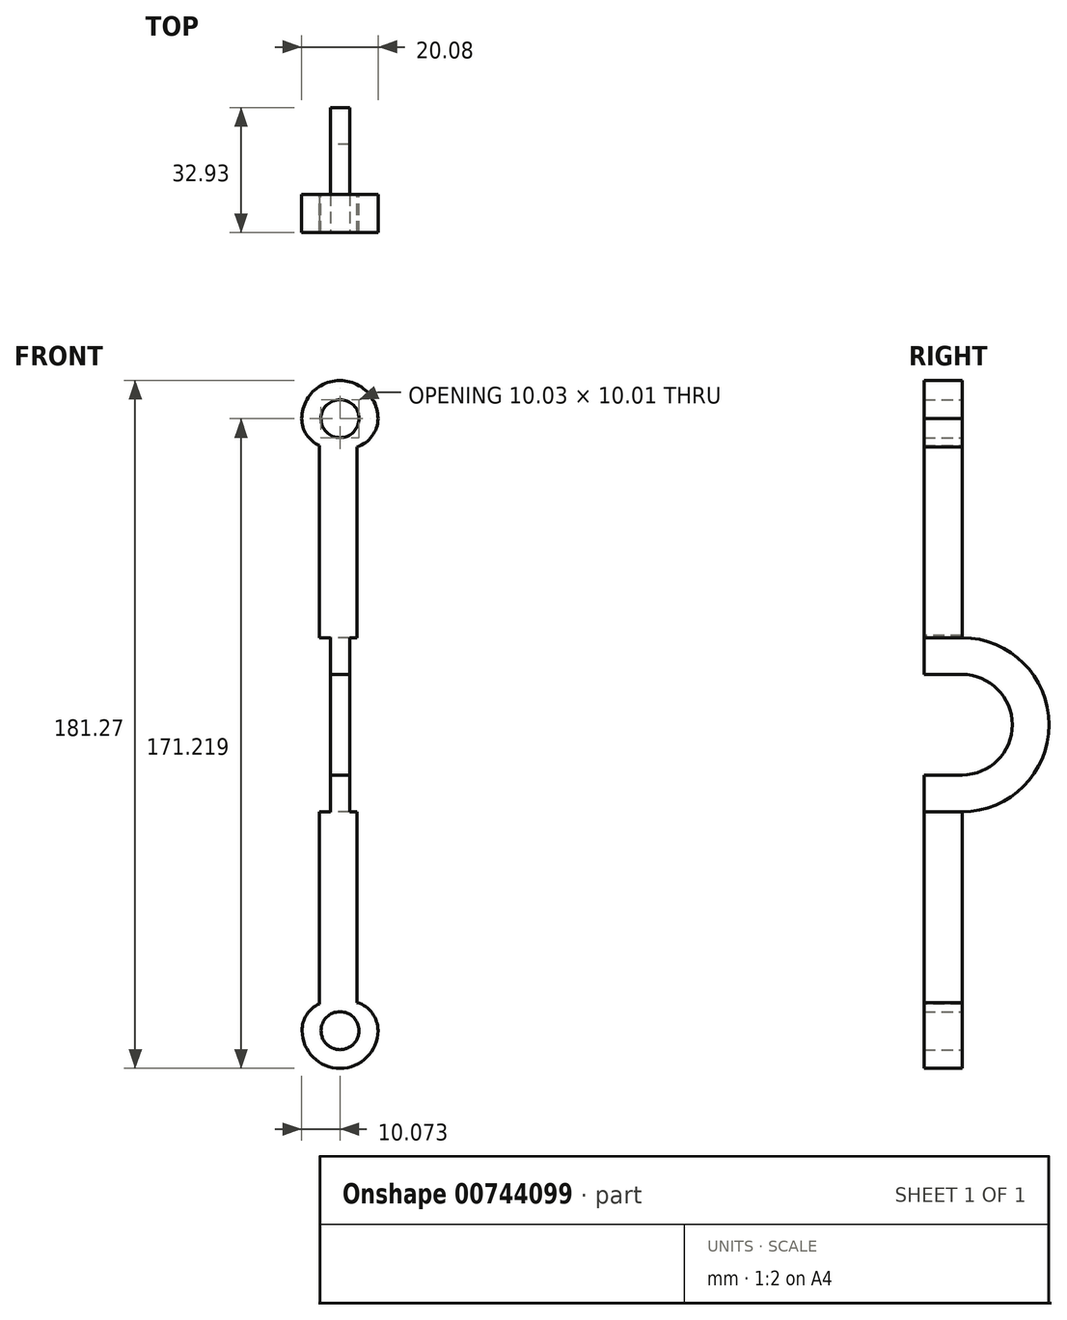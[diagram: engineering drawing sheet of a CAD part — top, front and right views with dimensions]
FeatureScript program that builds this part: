
annotation { "Feature Type Name" : "Feature", "Feature Type Description" : "" }
export const myFeature = defineFeature(function(context is Context, id is Id, definition is map)
    precondition{}
    {
        {
            var Q0;
            Q0=qCreatedBy(makeId("Right.planeOp"),FACE);
            var sketch = newSketch(context, id + "F0", { "sketchPlane" : qUnion([Q0])});
            skLineSegment(sketch, "E0", {"start": v(0, 45.86) * mm, "end": v(0, 36.18) * mm});
            skLineSegment(sketch, "E1", {"start": v(0, 0) * mm, "end": v(0, 9.68) * mm});
            skArc(sketch, "E2", {"start": v(0, 9.68) * mm, "mid": v(13.25, 22.93) * mm, "end": v(0, 36.18) * mm});
            skArc(sketch, "E3", {"start": v(0, 0) * mm, "mid": v(22.93, 22.93) * mm, "end": v(0, 45.86) * mm});
            skLineSegment(sketch, "E4", {"start": v(0, 45.86) * mm, "end": v(0, 95.86) * mm});
            skLineSegment(sketch, "E5", {"start": v(0, 0) * mm, "end": v(0, -50) * mm});
            skLineSegment(sketch, "E6", {"start": v(0, 36.18) * mm, "end": v(0, 9.68) * mm});
            skPoint(sketch, "E7.endSnap0", {"position": v(0, 41.02) * mm});
            skLineSegment(sketch, "E8", {"start": v(0, 9.68) * mm, "end": v(-10, 9.68) * mm});
            skLineSegment(sketch, "E9", {"start": v(0, 0) * mm, "end": v(-10, 0) * mm});
            skLineSegment(sketch, "E10", {"start": v(0, 36.18) * mm, "end": v(-10, 36.18) * mm});
            skLineSegment(sketch, "E11", {"start": v(0, 45.86) * mm, "end": v(-10, 45.86) * mm});
            skLineSegment(sketch, "E12", {"start": v(-10, 45.86) * mm, "end": v(-10, 36.18) * mm});
            skLineSegment(sketch, "E13", {"start": v(-10, 9.68) * mm, "end": v(-10, 0) * mm});
            skLineSegment(sketch, "E14", {"start": v(-10, 0) * mm, "end": v(-10, -50) * mm});
            skLineSegment(sketch, "E15", {"start": v(0, -50) * mm, "end": v(-10, -50) * mm});
            skPoint(sketch, "E16.start.orphan", {"position": v(3.95, 0.34) * mm});
            skPoint(sketch, "E17.end.orphan", {"position": v(3.95, -50) * mm});
            skLineSegment(sketch, "E18", {"start": v(-10, 45.86) * mm, "end": v(-10, 95.86) * mm});
            skLineSegment(sketch, "E19", {"start": v(-10, 95.86) * mm, "end": v(0, 95.86) * mm});
            skPoint(sketch, "E20.end.orphan", {"position": v(3.95, 95.86) * mm});
            skSolve(sketch);
        }
        {
            var Q0;
            Q0=makeQuery(id+"F0.imprint","IMPRINT",FACE,{"disambiguationData":[TD([[makeQuery(id+"F0.imprint","IMPRINT",EDGE,{"derivedFrom":sQuery(id+"F0.wireOp",EDGE,"E0")}),1.0]])]});
            var Q1;
            Q1=makeQuery(id+"F0.imprint","IMPRINT",FACE,{"disambiguationData":[TD([[makeQuery(id+"F0.imprint","IMPRINT",EDGE,{"derivedFrom":sQuery(id+"F0.wireOp",EDGE,"E5")}),-1.0]])]});
            var Q2;
            Q2=makeQuery(id+"F0.imprint","IMPRINT",FACE,{"disambiguationData":[TD([[makeQuery(id+"F0.imprint","IMPRINT",EDGE,{"derivedFrom":sQuery(id+"F0.wireOp",EDGE,"E1")}),1.0]])]});
            var Q3;
            Q3=makeQuery(id+"F0.imprint","IMPRINT",FACE,{"disambiguationData":[TD([[makeQuery(id+"F0.imprint","IMPRINT",EDGE,{"derivedFrom":sQuery(id+"F0.wireOp",EDGE,"E0")}),-1.0]])]});
            var Q4;
            Q4=makeQuery(id+"F0.imprint","IMPRINT",FACE,{"disambiguationData":[TD([[makeQuery(id+"F0.imprint","IMPRINT",EDGE,{"derivedFrom":sQuery(id+"F0.wireOp",EDGE,"E4")}),1.0]])]});
            extrude(context, id + "F1", {"entities" : qUnion([Q0, Q1, Q2, Q3, Q4]), "depth" : 4 * mm, "offsetDistance" : 25 * mm});
        }
        {
            var Q0;
            {var subQ0=sQuery(id+"F0.wireOp",EDGE,"E4");Q0=makeQuery(id+"F0.imprint","IMPRINT",FACE,{"disambiguationData":[TD([[makeQuery(id+"F0.imprint","IMPRINT",EDGE,{"derivedFrom":subQ0}),-1.0]])]});}
            var Q1;
            {var subQ0=sQuery(id+"F0.wireOp",EDGE,"E5");Q1=makeQuery(id+"F0.imprint","IMPRINT",FACE,{"disambiguationData":[TD([[makeQuery(id+"F0.imprint","IMPRINT",EDGE,{"derivedFrom":subQ0}),1.0]])]});}
            var Q2;
            {var subQ3=sQuery(id+"F0.wireOp",EDGE,"E0");Q2=makeQuery(id+"F0.imprint","IMPRINT",FACE,{"disambiguationData":[TD([[makeQuery(id+"F0.imprint","IMPRINT",EDGE,{"derivedFrom":subQ3}),1.0]])]});}
            extrude(context, id + "F2", {"entities" : qUnion([Q0, Q1, Q2]), "operationType" : NewBodyOperationType.ADD, "depth" : 5 * mm, "offsetDistance" : 25 * mm});
        }
        {
            var Q0;
            Q0=qCreatedBy(makeId("Front.planeOp"),FACE);
            var sketch = newSketch(context, id + "F3", { "sketchPlane" : qUnion([Q0])});
            skLineSegment(sketch, "E21", {"start": v(7.5, 103.58) * mm, "end": v(12.5, 103.58) * mm});
            skLineSegment(sketch, "E22", {"start": v(-2.52, 103.58) * mm, "end": v(-7.58, 103.58) * mm});
            skArc(sketch, "E23", {"start": v(-7.58, 103.58) * mm, "mid": v(-5.36, 98.18) * mm, "end": v(0, 95.86) * mm});
            skArc(sketch, "E24", {"start": v(5.02, 95.83) * mm, "mid": v(10.3, 98.22) * mm, "end": v(12.5, 103.58) * mm});
            skArc(sketch, "E25", {"start": v(-2.52, 103.58) * mm, "mid": v(2.5, 98.58) * mm, "end": v(7.5, 103.58) * mm});
            skLineSegment(sketch, "E26", {"start": v(0, 95.86) * mm, "end": v(5.02, 95.83) * mm});
            skLineSegment(sketch, "E27", {"start": v(-2.5, -57.69) * mm, "end": v(-7.5, -57.69) * mm});
            skLineSegment(sketch, "E28", {"start": v(7.48, -57.69) * mm, "end": v(12.5, -57.69) * mm});
            skArc(sketch, "E29", {"start": v(0, -49.95) * mm, "mid": v(-5.34, -52.28) * mm, "end": v(-7.5, -57.69) * mm});
            skArc(sketch, "E30", {"start": v(12.5, -57.69) * mm, "mid": v(10.28, -52.25) * mm, "end": v(4.88, -49.95) * mm});
            skArc(sketch, "E31", {"start": v(7.48, -57.69) * mm, "mid": v(2.49, -52.7) * mm, "end": v(-2.5, -57.69) * mm});
            skLineSegment(sketch, "E32", {"start": v(0, -49.95) * mm, "end": v(4.88, -49.95) * mm});
            skArc(sketch, "E33", {"start": v(-2.5, -57.69) * mm, "mid": v(2.49, -62.7) * mm, "end": v(7.48, -57.69) * mm});
            skArc(sketch, "E34", {"start": v(-7.5, -57.69) * mm, "mid": v(2.5, -67.63) * mm, "end": v(12.5, -57.69) * mm});
            skArc(sketch, "E35", {"start": v(7.5, 103.58) * mm, "mid": v(2.5, 108.6) * mm, "end": v(-2.52, 103.58) * mm});
            skArc(sketch, "E36", {"start": v(12.5, 103.58) * mm, "mid": v(2.46, 113.64) * mm, "end": v(-7.58, 103.58) * mm});
            skSolve(sketch);
        }
        {
            var Q0;
            Q0=makeQuery(id+"F3.imprint","IMPRINT",FACE,{"disambiguationData":[TD([[makeQuery(id+"F3.imprint","IMPRINT",EDGE,{"derivedFrom":sQuery(id+"F3.wireOp",EDGE,"E27")}),-1.0]])]});
            var Q1;
            Q1=makeQuery(id+"F3.imprint","IMPRINT",FACE,{"disambiguationData":[TD([[makeQuery(id+"F3.imprint","IMPRINT",EDGE,{"derivedFrom":sQuery(id+"F3.wireOp",EDGE,"E21")}),-1.0]])]});
            var Q2;
            Q2=makeQuery(id+"F3.imprint","IMPRINT",FACE,{"disambiguationData":[TD([[makeQuery(id+"F3.imprint","IMPRINT",EDGE,{"derivedFrom":sQuery(id+"F3.wireOp",EDGE,"E21")}),1.0]])]});
            var Q3;
            Q3=makeQuery(id+"F1.opExtrude","SWEPT_FACE",FACE,{"disambiguationData":[OSD([sQuery(id+"F0.wireOp",EDGE,"E13"),sQuery(id+"F0.wireOp",EDGE,"E14")])]});
            var Q4;
            Q4=makeQuery(id+"F1.opExtrude","SWEPT_FACE",FACE,{"disambiguationData":[OSD([sQuery(id+"F0.wireOp",EDGE,"E12"),sQuery(id+"F0.wireOp",EDGE,"E18")])]});
            extrude(context, id + "F4", {"entities" : qUnion([Q0, Q1, Q2]), "operationType" : NewBodyOperationType.ADD, "endBound" : BoundingType.UP_TO_SURFACE, "depth" : 0 * mm, "endBoundEntityFace" : qUnion([Q3]), "offsetDistance" : 25 * mm});
        }
        {
            var Q0;
            Q0=makeQuery(id+"F0.imprint","IMPRINT",FACE,{"disambiguationData":[TD([[makeQuery(id+"F0.imprint","IMPRINT",EDGE,{"derivedFrom":sQuery(id+"F0.wireOp",EDGE,"E1")}),1.0]])]});
            var Q1;
            {var subQ3=sQuery(id+"F0.wireOp",EDGE,"E0");Q1=makeQuery(id+"F0.imprint","IMPRINT",FACE,{"disambiguationData":[TD([[makeQuery(id+"F0.imprint","IMPRINT",EDGE,{"derivedFrom":subQ3}),1.0]])]});}
            var Q2;
            Q2=makeQuery(id+"F0.imprint","IMPRINT",FACE,{"disambiguationData":[TD([[makeQuery(id+"F0.imprint","IMPRINT",EDGE,{"derivedFrom":sQuery(id+"F0.wireOp",EDGE,"E0")}),-1.0]])]});
            var Q3;
            {var subQ0=sQuery(id+"F0.wireOp",EDGE,"E4");Q3=makeQuery(id+"F0.imprint","IMPRINT",FACE,{"disambiguationData":[TD([[makeQuery(id+"F0.imprint","IMPRINT",EDGE,{"derivedFrom":subQ0}),-1.0]])]});}
            var Q4;
            {var subQ0=sQuery(id+"F0.wireOp",EDGE,"E5");Q4=makeQuery(id+"F0.imprint","IMPRINT",FACE,{"disambiguationData":[TD([[makeQuery(id+"F0.imprint","IMPRINT",EDGE,{"derivedFrom":subQ0}),1.0]])]});}
            extrude(context, id + "F5", {"entities" : qUnion([Q0, Q1, Q2, Q3, Q4]), "operationType" : NewBodyOperationType.ADD, "depth" : 5 * mm, "offsetDistance" : 25 * mm});
        }
        {
            var Q0;
            Q0=makeQuery(id+"F3.imprint","IMPRINT",FACE,{"disambiguationData":[TD([[makeQuery(id+"F3.imprint","IMPRINT",EDGE,{"derivedFrom":sQuery(id+"F3.wireOp",EDGE,"E27")}),1.0]])]});
            extrude(context, id + "F6", {"entities" : qUnion([Q0]), "operationType" : NewBodyOperationType.ADD, "depth" : 10 * mm, "offsetDistance" : 25 * mm});
        }
        {
            var Q0;
            Q0=makeQuery(id+"F0.imprint","IMPRINT",FACE,{"disambiguationData":[TD([[makeQuery(id+"F0.imprint","IMPRINT",EDGE,{"derivedFrom":sQuery(id+"F0.wireOp",EDGE,"E0")}),1.0]])]});
            var Q1;
            Q1=makeQuery(id+"F0.imprint","IMPRINT",FACE,{"disambiguationData":[TD([[makeQuery(id+"F0.imprint","IMPRINT",EDGE,{"derivedFrom":sQuery(id+"F0.wireOp",EDGE,"E1")}),1.0]])]});
            var Q2;
            Q2=makeQuery(id+"F0.imprint","IMPRINT",FACE,{"disambiguationData":[TD([[makeQuery(id+"F0.imprint","IMPRINT",EDGE,{"derivedFrom":sQuery(id+"F0.wireOp",EDGE,"E0")}),-1.0]])]});
            extrude(context, id + "F7", {"entities" : qUnion([Q0, Q1, Q2]), "operationType" : NewBodyOperationType.ADD, "depth" : 4 * mm, "offsetDistance" : 25 * mm});
        }
        {
            var Q0;
            {var subQ0=sQuery(id+"F3.wireOp",EDGE,"E28");var subQ1=sQuery(id+"F3.wireOp",EDGE,"E27");var subQ2=sQuery(id+"F0.wireOp",EDGE,"E13");Q0=makeQuery(id+"F6.boolean.opBoolean","MERGE",FACE,{"derivedFrom":[makeQuery(id+"F5.boolean.opBoolean","MERGE",FACE,{"derivedFrom":[makeQuery(id+"F4.boolean.opBoolean","MERGE",FACE,{"derivedFrom":[makeQuery(id+"F1.opExtrude","SWEPT_FACE",FACE,{"disambiguationData":[OSD([subQ2,sQuery(id+"F0.wireOp",EDGE,"E14")])]}),makeQuery(id+"F4.opExtrude","CAP_FACE",FACE,{"disambiguationData":[OSD([subQ1,subQ0,sQuery(id+"F3.wireOp",EDGE,"E29"),sQuery(id+"F3.wireOp",EDGE,"E30"),sQuery(id+"F3.wireOp",EDGE,"E31"),sQuery(id+"F3.wireOp",EDGE,"E32")])],"isStart":false})]}),makeQuery(id+"F5.opExtrude","SWEPT_FACE",FACE,{"disambiguationData":[OSD([subQ2])]})]}),makeQuery(id+"F6.opExtrude","CAP_FACE",FACE,{"disambiguationData":[OSD([subQ1,subQ0,sQuery(id+"F3.wireOp",EDGE,"E33"),sQuery(id+"F3.wireOp",EDGE,"E34")])],"isStart":false})]});}
            var sketch = newSketch(context, id + "F8", { "sketchPlane" : qUnion([Q0])});
            skLineSegment(sketch, "E37", {"start": v(-3, -2.45) * mm, "end": v(-3, -50.63) * mm});
            skLineSegment(sketch, "E38", {"start": v(7, -2.45) * mm, "end": v(7, -49.95) * mm});
            skLineSegment(sketch, "E39", {"start": v(-3, -2.45) * mm, "end": v(7, -2.45) * mm});
            skLineSegment(sketch, "E40", {"start": v(7, 63.85) * mm, "end": v(7, 46.07) * mm});
            skLineSegment(sketch, "E41", {"start": v(-3, 63.85) * mm, "end": v(-3, 46.44) * mm});
            skLineSegment(sketch, "E42", {"start": v(7, -49.95) * mm, "end": v(7, -50.27) * mm});
            skLineSegment(sketch, "E43", {"start": v(-3, 63.85) * mm, "end": v(-3, 95.87) * mm});
            skLineSegment(sketch, "E44", {"start": v(7, 63.85) * mm, "end": v(7, 95.87) * mm});
            skLineSegment(sketch, "E45", {"start": v(-3, 95.87) * mm, "end": v(-3, 96.56) * mm});
            skLineSegment(sketch, "E46", {"start": v(7, 95.87) * mm, "end": v(7, 96.56) * mm});
            skLineSegment(sketch, "E47", {"start": v(7, 96.56) * mm, "end": v(-3, 96.56) * mm});
            skLineSegment(sketch, "E48", {"start": v(7, -2.45) * mm, "end": v(7, 0) * mm});
            skLineSegment(sketch, "E49", {"start": v(-3, -2.45) * mm, "end": v(-3, 0) * mm});
            skLineSegment(sketch, "E50", {"start": v(-3, 0) * mm, "end": v(7, 0) * mm});
            skLineSegment(sketch, "E51", {"start": v(7, 46.07) * mm, "end": v(7, 45.82) * mm});
            skLineSegment(sketch, "E52", {"start": v(7, 45.82) * mm, "end": v(-3, 45.82) * mm});
            skLineSegment(sketch, "E53", {"start": v(-3, 46.44) * mm, "end": v(-3, 45.82) * mm});
            skLineSegment(sketch, "E54", {"start": v(0, 46.44) * mm, "end": v(0, 45.82) * mm});
            skLineSegment(sketch, "E55", {"start": v(3.94, 46.44) * mm, "end": v(3.94, 45.82) * mm});
            skSolve(sketch);
        }
        {
            var Q0;
            {var subQ2=sQuery(id+"F8.wireOp",EDGE,"E38");Q0=makeQuery(id+"F8.imprint","IMPRINT",FACE,{"disambiguationData":[TD([[makeQuery(id+"F8.imprint","IMPRINT",EDGE,{"derivedFrom":subQ2}),-1.0]])]});}
            var Q1;
            {var subQ0=sQuery(id+"F3.wireOp",EDGE,"E28");var subQ1=sQuery(id+"F3.wireOp",EDGE,"E27");Q1=makeQuery(id+"F6.boolean.opBoolean","MERGE",FACE,{"derivedFrom":[makeQuery(id+"F4.boolean.opBoolean","MERGE",FACE,{"derivedFrom":[makeQuery(id+"F1.opExtrude","SWEPT_FACE",FACE,{"disambiguationData":[OSD([sQuery(id+"F0.wireOp",EDGE,"E5")])]}),makeQuery(id+"F4.opExtrude","CAP_FACE",FACE,{"disambiguationData":[OSD([subQ1,subQ0,sQuery(id+"F3.wireOp",EDGE,"E29"),sQuery(id+"F3.wireOp",EDGE,"E30"),sQuery(id+"F3.wireOp",EDGE,"E31"),sQuery(id+"F3.wireOp",EDGE,"E32")])],"isStart":true})]}),makeQuery(id+"F6.opExtrude","CAP_FACE",FACE,{"disambiguationData":[OSD([subQ1,subQ0,sQuery(id+"F3.wireOp",EDGE,"E33"),sQuery(id+"F3.wireOp",EDGE,"E34")])],"isStart":true})]});}
            extrude(context, id + "F9", {"entities" : qUnion([Q0]), "operationType" : NewBodyOperationType.ADD, "endBound" : BoundingType.UP_TO_SURFACE, "oppositeDirection" : true, "depth" : 25 * mm, "endBoundEntityFace" : qUnion([Q1]), "offsetDistance" : 25 * mm});
        }
        {
            var Q0;
            {var subQ0=sQuery(id+"F8.wireOp",EDGE,"E37");Q0=makeQuery(id+"F8.imprint","IMPRINT",FACE,{"disambiguationData":[TD([[makeQuery(id+"F8.imprint","IMPRINT",EDGE,{"derivedFrom":subQ0}),1.0]])]});}
            var Q1;
            {var subQ0=sQuery(id+"F3.wireOp",EDGE,"E32");var subQ1=sQuery(id+"F3.wireOp",EDGE,"E30");var subQ2=sQuery(id+"F3.wireOp",EDGE,"E28");var subQ3=sQuery(id+"F3.wireOp",EDGE,"E27");Q1=makeQuery(id+"F9.boolean.opBoolean","MERGE",FACE,{"derivedFrom":[makeQuery(id+"F6.boolean.opBoolean","MERGE",FACE,{"derivedFrom":[makeQuery(id+"F4.boolean.opBoolean","MERGE",FACE,{"derivedFrom":[makeQuery(id+"F1.opExtrude","SWEPT_FACE",FACE,{"disambiguationData":[OSD([sQuery(id+"F0.wireOp",EDGE,"E5")])]}),makeQuery(id+"F4.opExtrude","CAP_FACE",FACE,{"disambiguationData":[OSD([subQ3,subQ2,sQuery(id+"F3.wireOp",EDGE,"E29"),subQ1,sQuery(id+"F3.wireOp",EDGE,"E31"),subQ0])],"isStart":true})]}),makeQuery(id+"F6.opExtrude","CAP_FACE",FACE,{"disambiguationData":[OSD([subQ3,subQ2,sQuery(id+"F3.wireOp",EDGE,"E33"),sQuery(id+"F3.wireOp",EDGE,"E34")])],"isStart":true})]}),makeQuery(id+"F9.opExtrude","CAP_FACE",FACE,{"disambiguationData":[OSD([sQuery(id+"F0.wireOp",EDGE,"E13"),sQuery(id+"F0.wireOp",EDGE,"E14"),subQ1,subQ0,sQuery(id+"F8.wireOp",EDGE,"E38"),sQuery(id+"F8.wireOp",EDGE,"E39"),sQuery(id+"F8.wireOp",EDGE,"E42")])],"isStart":false})]});}
            extrude(context, id + "F10", {"entities" : qUnion([Q0]), "operationType" : NewBodyOperationType.ADD, "endBound" : BoundingType.UP_TO_SURFACE, "oppositeDirection" : true, "depth" : 25 * mm, "endBoundEntityFace" : qUnion([Q1]), "offsetDistance" : 25 * mm});
        }
        {
            var Q0;
            Q0=makeQuery(id+"F8.imprint","IMPRINT",FACE,{"disambiguationData":[TD([[makeQuery(id+"F8.imprint","IMPRINT",EDGE,{"derivedFrom":sQuery(id+"F8.wireOp",EDGE,"E41")}),1.0]])]});
            var Q1;
            Q1=makeQuery(id+"F4.boolean.opBoolean","MERGE",FACE,{"derivedFrom":[makeQuery(id+"F1.opExtrude","SWEPT_FACE",FACE,{"disambiguationData":[OSD([sQuery(id+"F0.wireOp",EDGE,"E4")])]}),makeQuery(id+"F4.opExtrude","CAP_FACE",FACE,{"disambiguationData":[OSD([sQuery(id+"F3.wireOp",EDGE,"E23"),sQuery(id+"F3.wireOp",EDGE,"E24"),sQuery(id+"F3.wireOp",EDGE,"E25"),sQuery(id+"F3.wireOp",EDGE,"E26"),sQuery(id+"F3.wireOp",EDGE,"E35"),sQuery(id+"F3.wireOp",EDGE,"E36")])],"isStart":true})]});
            extrude(context, id + "F11", {"entities" : qUnion([Q0]), "operationType" : NewBodyOperationType.ADD, "endBound" : BoundingType.UP_TO_SURFACE, "oppositeDirection" : true, "depth" : 25 * mm, "endBoundEntityFace" : qUnion([Q1]), "offsetDistance" : 25 * mm});
        }
        {
            var Q0;
            {var subQ3=sQuery(id+"F8.wireOp",EDGE,"E48");Q0=makeQuery(id+"F8.imprint","IMPRINT",FACE,{"disambiguationData":[TD([[makeQuery(id+"F8.imprint","IMPRINT",EDGE,{"derivedFrom":subQ3}),1.0]])]});}
            var Q1;
            {var subQ0=sQuery(id+"F8.wireOp",EDGE,"E49");Q1=makeQuery(id+"F8.imprint","IMPRINT",FACE,{"disambiguationData":[TD([[makeQuery(id+"F8.imprint","IMPRINT",EDGE,{"derivedFrom":subQ0}),-1.0]])]});}
            var Q2;
            {var subQ0=sQuery(id+"F8.wireOp",EDGE,"E39");var subQ1=sQuery(id+"F3.wireOp",EDGE,"E29");var subQ2=sQuery(id+"F0.wireOp",EDGE,"E14");var subQ3=sQuery(id+"F0.wireOp",EDGE,"E13");var subQ4=sQuery(id+"F3.wireOp",EDGE,"E32");var subQ5=sQuery(id+"F3.wireOp",EDGE,"E30");var subQ6=sQuery(id+"F3.wireOp",EDGE,"E28");var subQ7=sQuery(id+"F3.wireOp",EDGE,"E27");Q2=makeQuery(id+"F10.boolean.opBoolean","MERGE",FACE,{"derivedFrom":[makeQuery(id+"F9.boolean.opBoolean","MERGE",FACE,{"derivedFrom":[makeQuery(id+"F6.boolean.opBoolean","MERGE",FACE,{"derivedFrom":[makeQuery(id+"F4.boolean.opBoolean","MERGE",FACE,{"derivedFrom":[makeQuery(id+"F1.opExtrude","SWEPT_FACE",FACE,{"disambiguationData":[OSD([sQuery(id+"F0.wireOp",EDGE,"E5")])]}),makeQuery(id+"F4.opExtrude","CAP_FACE",FACE,{"disambiguationData":[OSD([subQ7,subQ6,subQ1,subQ5,sQuery(id+"F3.wireOp",EDGE,"E31"),subQ4])],"isStart":true})]}),makeQuery(id+"F6.opExtrude","CAP_FACE",FACE,{"disambiguationData":[OSD([subQ7,subQ6,sQuery(id+"F3.wireOp",EDGE,"E33"),sQuery(id+"F3.wireOp",EDGE,"E34")])],"isStart":true})]}),makeQuery(id+"F9.opExtrude","CAP_FACE",FACE,{"disambiguationData":[OSD([subQ3,subQ2,subQ5,subQ4,sQuery(id+"F8.wireOp",EDGE,"E38"),subQ0,sQuery(id+"F8.wireOp",EDGE,"E42")])],"isStart":false})]}),makeQuery(id+"F10.opExtrude","CAP_FACE",FACE,{"disambiguationData":[OSD([subQ3,subQ2,subQ1,sQuery(id+"F8.wireOp",EDGE,"E37"),subQ0])],"isStart":false})]});}
            extrude(context, id + "F12", {"entities" : qUnion([Q0, Q1]), "operationType" : NewBodyOperationType.ADD, "endBound" : BoundingType.UP_TO_SURFACE, "oppositeDirection" : true, "depth" : 25 * mm, "endBoundEntityFace" : qUnion([Q2]), "offsetDistance" : 25 * mm});
        }
    });
